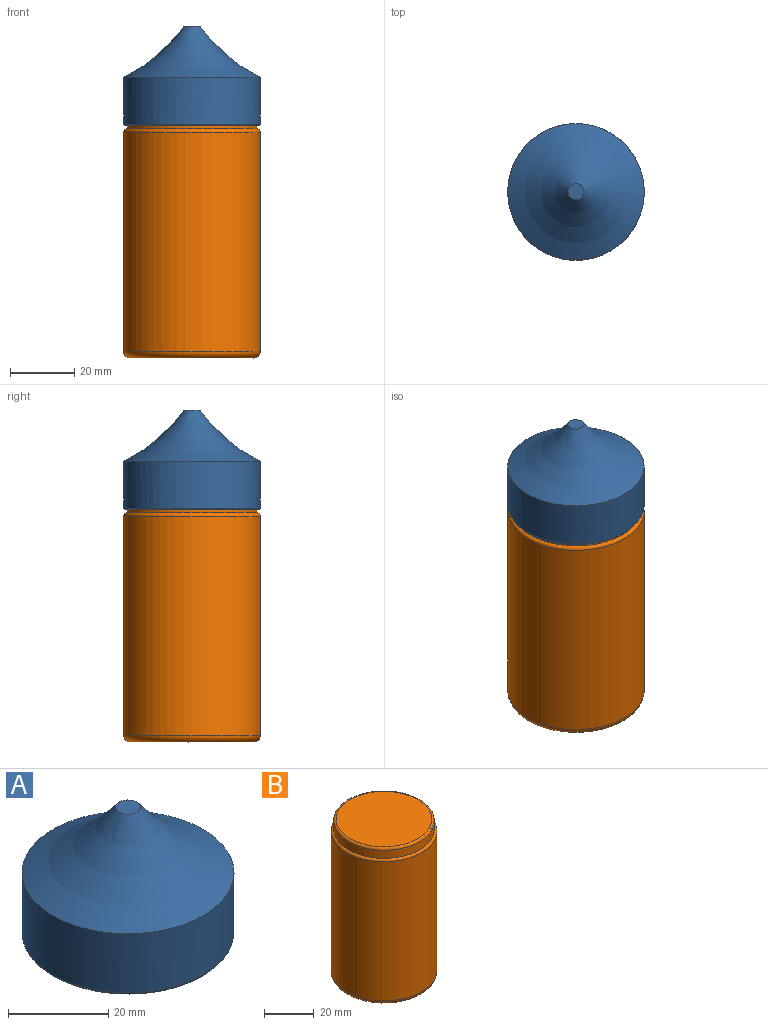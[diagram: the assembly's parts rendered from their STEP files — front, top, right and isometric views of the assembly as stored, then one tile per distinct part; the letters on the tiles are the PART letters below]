
ASSEMBLY  parts=2 mates=1
PART A: 7 faces, bbox 45.9x45.9x31 mm
  f0: plane 41.4x41.4mm, normal (0,0,-1), area 328.3mm2, adj f4,f6
  f1: cylinder r=21.2mm len=42.4mm, axis (0,0,-1), area 1931.5mm2, adj f2,f6
  f2: torus R=43.36mm, axis (0,0,-1), area 1747.4mm2, adj f1,f3
  f3: plane 5x5mm, normal (0,0,1), area 19.6mm2, adj f2
  f4: cylinder r=18mm len=36mm, axis (0,0,1), area 1696.5mm2, adj f0,f5
  f5: plane 36x36mm, normal (0,0,-1), area 1017.9mm2, adj f4
  f6: torus R=20.7mm, axis (0,0,1), area 103.7mm2, adj f0,f1
PART B: 7 faces, bbox 45.9x45.9x76.2 mm
  f0: torus R=19.2mm, axis (0,0,-1), area 404.1mm2, adj f1,f5
  f1: cylinder r=21.2mm len=68.2mm, axis (0,0,-1), area 9084.5mm2, adj f0,f2
  f2: torus R=20.2mm, axis (0,0,-1), area 205.6mm2, adj f1,f3
  f3: cylinder r=20.2mm len=40.4mm, axis (0,0,-1), area 507.7mm2, adj f2,f6
  f4: plane 38.4x38.4mm, normal (0,0,1), area 1158.1mm2, adj f6
  f5: plane 38.4x38.4mm, normal (0,0,-1), area 1158.1mm2, adj f0
  f6: torus R=19.2mm, axis (0,0,1), area 195.8mm2, adj f3,f4
PLACE A rot(axis=(-0.03,0.83,0.56),0deg) t=(-3.57,-8.54,136.08)mm
PLACE B rot(axis=(-0.03,0.83,0.56),0deg) t=(-3.57,-8.54,48.88)mm
MATE slider A.f4 <-> B.f0  axis (0,0,1) through (-3.57,-8.54,121.08)mm
